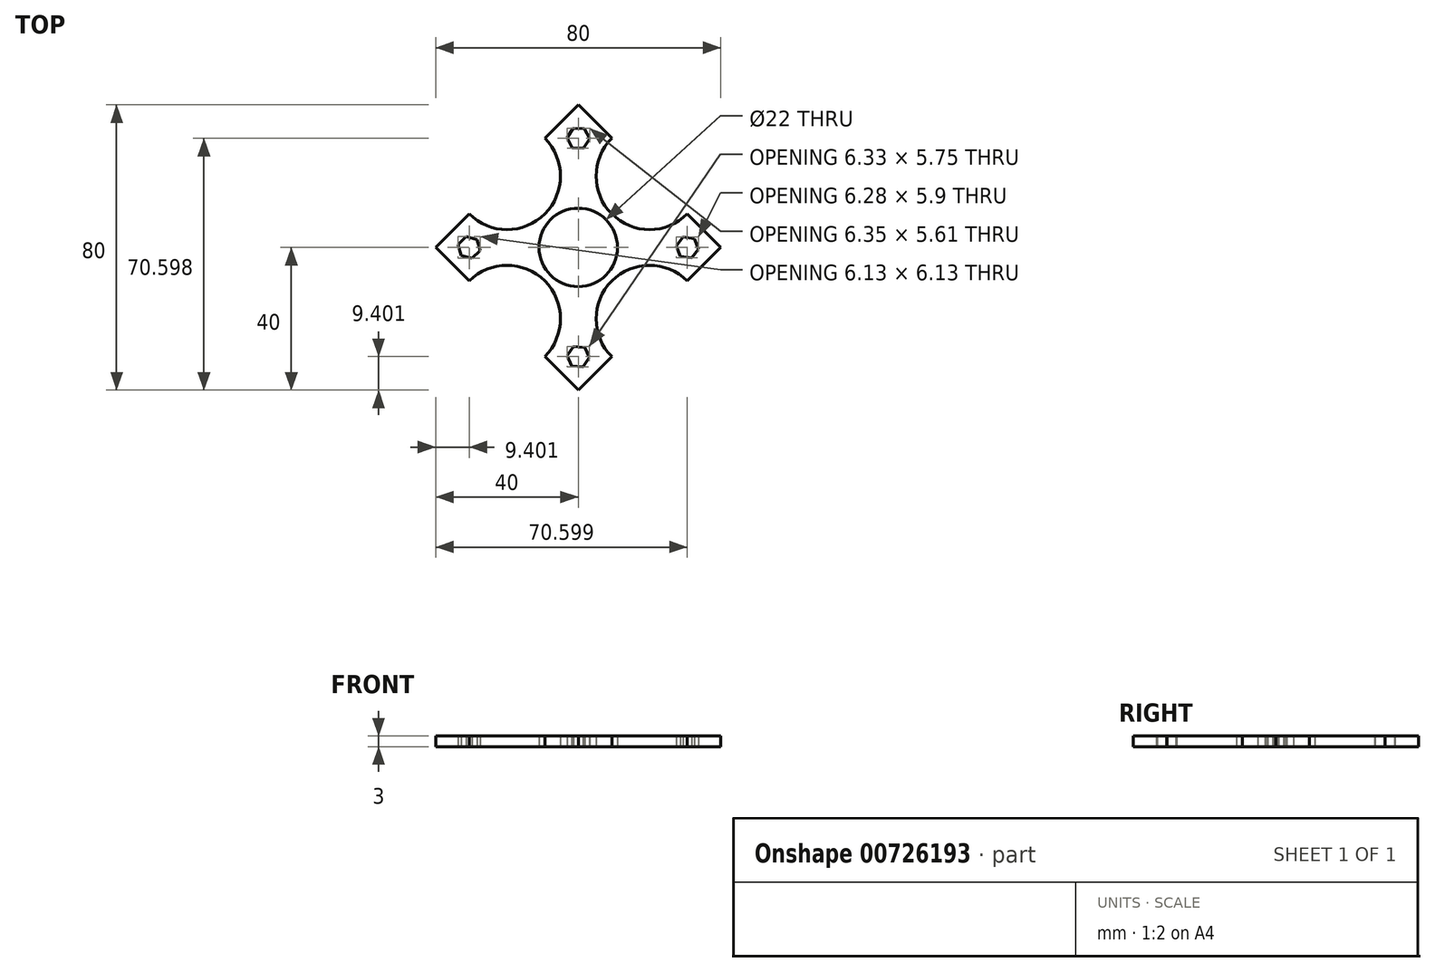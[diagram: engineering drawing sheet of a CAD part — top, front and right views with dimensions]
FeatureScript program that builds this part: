
annotation { "Feature Type Name" : "Feature", "Feature Type Description" : "" }
export const myFeature = defineFeature(function(context is Context, id is Id, definition is map)
    precondition{}
    {
        {
            var Q0;
            Q0=qCreatedBy(makeId("Top.planeOp"),FACE);
            var sketch = newSketch(context, id + "F0", { "sketchPlane" : qUnion([Q0])});
            skArc(sketch, "E0", {"start": v(11, 0) * mm, "mid": v(0, 11) * mm, "end": v(-11, 0) * mm});
            skLineSegment(sketch, "E1", {"start": v(0, 40) * mm, "end": v(9.4, 30.6) * mm});
            skArc(sketch, "E2", {"start": v(9.4, 30.6) * mm, "mid": v(9.4, 9.4) * mm, "end": v(30.6, 9.4) * mm});
            skLineSegment(sketch, "E3.trimOffspring", {"start": v(30.6, 9.4) * mm, "end": v(40, 0) * mm});
            skPoint(sketch, "E4.start.orphan", {"position": v(0, -20.73) * mm});
            skLineSegment(sketch, "E5.1.0", {"start": v(-40, 0) * mm, "end": v(-30.6, 9.4) * mm});
            skArc(sketch, "E5.1.1", {"start": v(-30.6, 9.4) * mm, "mid": v(-9.4, 9.4) * mm, "end": v(-9.4, 30.6) * mm});
            skLineSegment(sketch, "E5.1.6", {"start": v(-9.4, 30.6) * mm, "end": v(0, 40) * mm});
            skLineSegment(sketch, "E5.2.0", {"start": v(0, -40) * mm, "end": v(-9.4, -30.6) * mm});
            skArc(sketch, "E5.2.1", {"start": v(-9.4, -30.6) * mm, "mid": v(-9.4, -9.4) * mm, "end": v(-30.6, -9.4) * mm});
            skArc(sketch, "E5.2.4", {"start": v(-11, 0) * mm, "mid": v(0, -11) * mm, "end": v(11, 0) * mm});
            skLineSegment(sketch, "E5.2.6", {"start": v(-30.6, -9.4) * mm, "end": v(-40, 0) * mm});
            skLineSegment(sketch, "E5.3.0", {"start": v(40, 0) * mm, "end": v(30.6, -9.4) * mm});
            skArc(sketch, "E5.3.1", {"start": v(30.6, -9.4) * mm, "mid": v(9.4, -9.4) * mm, "end": v(9.4, -30.6) * mm});
            skLineSegment(sketch, "E5.3.6", {"start": v(9.4, -30.6) * mm, "end": v(0, -40) * mm});
            skLineSegment(sketch, "E6", {"start": v(-30.6, 2.85) * mm, "end": v(-30.6, 2.75) * mm});
            skLineSegment(sketch, "E7", {"start": v(-3.11, 30.6) * mm, "end": v(-2.75, 30.6) * mm});
            skLineSegment(sketch, "E8", {"start": v(30.6, 2.78) * mm, "end": v(30.6, 2.75) * mm});
            skLineSegment(sketch, "E9", {"start": v(3.04, -30.6) * mm, "end": v(2.75, -30.6) * mm});
            skCircle(sketch, "E10.cCircle", {"center": v(-30.6, 0) * mm, "radius": 2.75 * mm, "construction": true});
            skLineSegment(sketch, "E10.0", {"start": v(-33.67, 0.82) * mm, "end": v(-31.42, 3.07) * mm});
            skLineSegment(sketch, "E10.1", {"start": v(-31.42, 3.07) * mm, "end": v(-28.35, 2.25) * mm});
            skLineSegment(sketch, "E10.2", {"start": v(-28.35, 2.25) * mm, "end": v(-27.53, -0.82) * mm});
            skLineSegment(sketch, "E10.3", {"start": v(-27.53, -0.82) * mm, "end": v(-29.78, -3.07) * mm});
            skLineSegment(sketch, "E10.4", {"start": v(-29.78, -3.07) * mm, "end": v(-32.84, -2.25) * mm});
            skLineSegment(sketch, "E10.5", {"start": v(-32.84, -2.25) * mm, "end": v(-33.67, 0.82) * mm});
            skPoint(sketch, "E10.0.midPoint", {"position": v(-32.54, 1.94) * mm});
            skCircle(sketch, "E11.cCircle", {"center": v(0, 30.6) * mm, "radius": 2.75 * mm, "construction": true});
            skLineSegment(sketch, "E11.0", {"start": v(-3.17, 30.7) * mm, "end": v(-1.5, 33.4) * mm});
            skLineSegment(sketch, "E11.1", {"start": v(-1.5, 33.4) * mm, "end": v(1.68, 33.3) * mm});
            skLineSegment(sketch, "E11.2", {"start": v(1.68, 33.3) * mm, "end": v(3.17, 30.49) * mm});
            skLineSegment(sketch, "E11.3", {"start": v(3.17, 30.49) * mm, "end": v(1.5, 27.8) * mm});
            skLineSegment(sketch, "E11.4", {"start": v(1.5, 27.8) * mm, "end": v(-1.68, 27.9) * mm});
            skLineSegment(sketch, "E11.5", {"start": v(-1.68, 27.9) * mm, "end": v(-3.17, 30.7) * mm});
            skPoint(sketch, "E11.0.midPoint", {"position": v(-2.33, 32.06) * mm});
            skCircle(sketch, "E12.cCircle", {"center": v(30.6, 0) * mm, "radius": 2.75 * mm, "construction": true});
            skLineSegment(sketch, "E12.0", {"start": v(27.46, 0.46) * mm, "end": v(29.43, 2.95) * mm});
            skLineSegment(sketch, "E12.1", {"start": v(29.43, 2.95) * mm, "end": v(32.57, 2.49) * mm});
            skLineSegment(sketch, "E12.2", {"start": v(32.57, 2.49) * mm, "end": v(33.74, -0.46) * mm});
            skLineSegment(sketch, "E12.3", {"start": v(33.74, -0.46) * mm, "end": v(31.77, -2.95) * mm});
            skLineSegment(sketch, "E12.4", {"start": v(31.77, -2.95) * mm, "end": v(28.63, -2.49) * mm});
            skLineSegment(sketch, "E12.5", {"start": v(28.63, -2.49) * mm, "end": v(27.46, 0.46) * mm});
            skPoint(sketch, "E12.0.midPoint", {"position": v(28.44, 1.7) * mm});
            skCircle(sketch, "E13.cCircle", {"center": v(0, -30.6) * mm, "radius": 2.75 * mm, "construction": true});
            skLineSegment(sketch, "E13.0", {"start": v(-3.16, -30.33) * mm, "end": v(-1.35, -27.73) * mm});
            skLineSegment(sketch, "E13.1", {"start": v(-1.35, -27.73) * mm, "end": v(1.81, -28) * mm});
            skLineSegment(sketch, "E13.2", {"start": v(1.81, -28) * mm, "end": v(3.16, -30.86) * mm});
            skLineSegment(sketch, "E13.3", {"start": v(3.16, -30.86) * mm, "end": v(1.35, -33.47) * mm});
            skLineSegment(sketch, "E13.4", {"start": v(1.35, -33.47) * mm, "end": v(-1.81, -33.2) * mm});
            skLineSegment(sketch, "E13.5", {"start": v(-1.81, -33.2) * mm, "end": v(-3.16, -30.33) * mm});
            skPoint(sketch, "E13.0.midPoint", {"position": v(-2.26, -29.03) * mm});
            skLineSegment(sketch, "E14.trimOffspring", {"start": v(-30.6, -2.75) * mm, "end": v(-30.6, -2.85) * mm});
            skLineSegment(sketch, "E15.trimOffspring", {"start": v(-2.75, -30.6) * mm, "end": v(-3.04, -30.6) * mm});
            skLineSegment(sketch, "E16.trimOffspring", {"start": v(30.6, -2.75) * mm, "end": v(30.6, -2.78) * mm});
            skLineSegment(sketch, "E17.trimOffspring", {"start": v(2.75, 30.6) * mm, "end": v(3.11, 30.6) * mm});
            skSolve(sketch);
        }
        {
            var Q0;
            Q0 = qSketchRegion(id + "F0", true);
            extrude(context, id + "F1", {"entities" : qUnion([Q0]), "depth" : 3 * mm, "offsetDistance" : 25 * mm});
        }
    });
